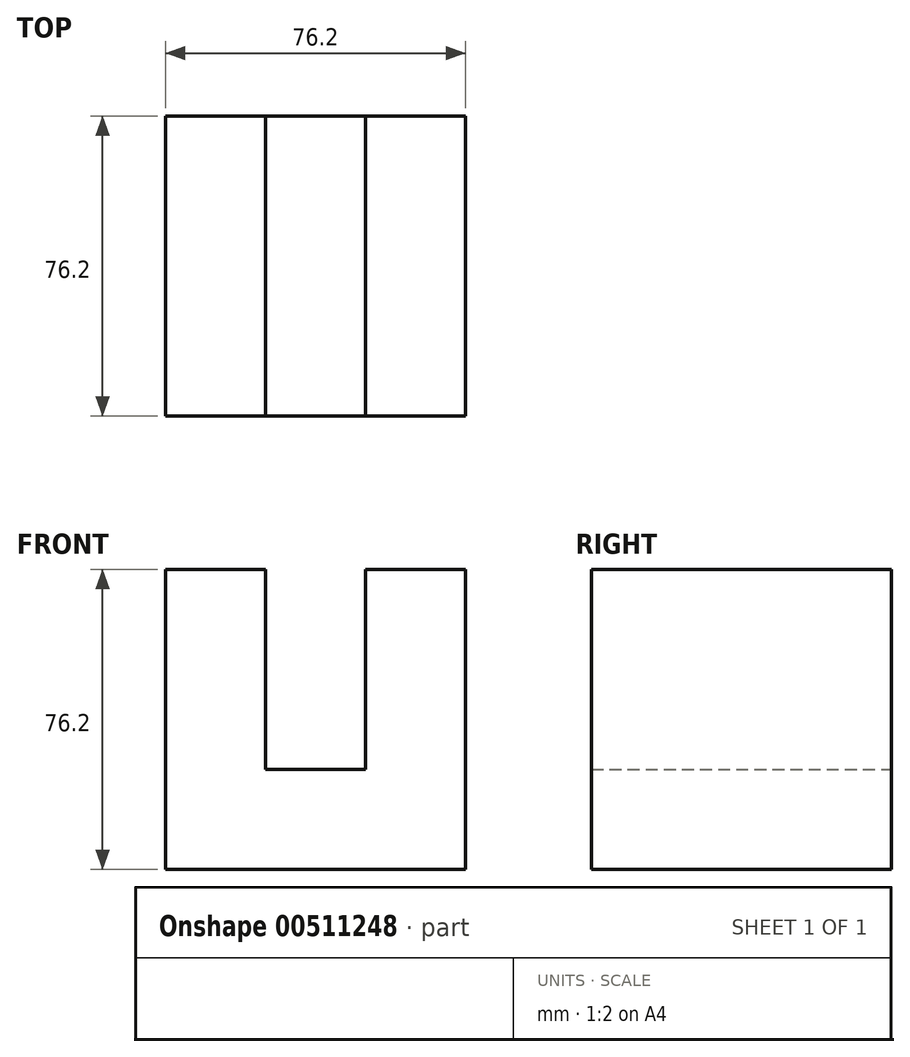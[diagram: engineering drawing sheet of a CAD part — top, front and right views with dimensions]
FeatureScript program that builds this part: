
annotation { "Feature Type Name" : "Feature", "Feature Type Description" : "" }
export const myFeature = defineFeature(function(context is Context, id is Id, definition is map)
    precondition{}
    {
        {
            var Q0;
            Q0=qCreatedBy(makeId("Front.planeOp"),FACE);
            var sketch = newSketch(context, id + "F0", { "sketchPlane" : qUnion([Q0])});
            skLineSegment(sketch, "E0", {"start": v(52.7, -9.85) * mm, "end": v(-23.5, -9.85) * mm});
            skLineSegment(sketch, "E1", {"start": v(-23.5, -9.85) * mm, "end": v(-23.5, 66.35) * mm});
            skLineSegment(sketch, "E2", {"start": v(-23.5, 66.35) * mm, "end": v(1.9, 66.35) * mm});
            skLineSegment(sketch, "E3", {"start": v(1.9, 66.35) * mm, "end": v(1.9, 15.55) * mm});
            skLineSegment(sketch, "E4", {"start": v(1.9, 15.55) * mm, "end": v(27.3, 15.55) * mm});
            skLineSegment(sketch, "E5", {"start": v(27.3, 15.55) * mm, "end": v(27.3, 66.35) * mm});
            skLineSegment(sketch, "E6", {"start": v(27.3, 66.35) * mm, "end": v(52.7, 66.35) * mm});
            skLineSegment(sketch, "E7", {"start": v(52.7, 66.35) * mm, "end": v(52.7, -9.85) * mm});
            skSolve(sketch);
        }
        {
            var Q0;
            Q0 = qSketchRegion(id + "F0", true);
            extrude(context, id + "F1", {"entities" : qUnion([Q0]), "depth" : 76.2 * mm});
        }
    });
